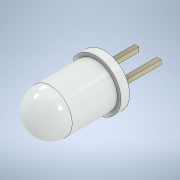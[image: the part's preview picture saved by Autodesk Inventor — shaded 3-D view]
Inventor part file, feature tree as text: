
AUTODESK INVENTOR PART (.ipt)
format: ipt  version: 2022 (Build 260153000, 153)  size: 149,504 bytes
history: native  units: mm
features: extrude x3, sketch x3, other x1, fillet x1
ambient origin geometry x8: Origin, YZ Plane, XZ Plane, XY Plane, X Axis, Y Axis, Z Axis, Center Point
bodies: Body1 (feature_tree)
feature tree (8):
  other  "ソリッド1"
  extrude  "押し出し1"  Depth=5.0mm
  fillet  "フィレット1"  Radius=7.7mm
  extrude  "押し出し2"  Depth=2.5mm
  extrude  "押し出し3"  Depth=5.8mm
  sketch  "スケッチ1"
  sketch  "スケッチ2"
  sketch  "スケッチ3"
